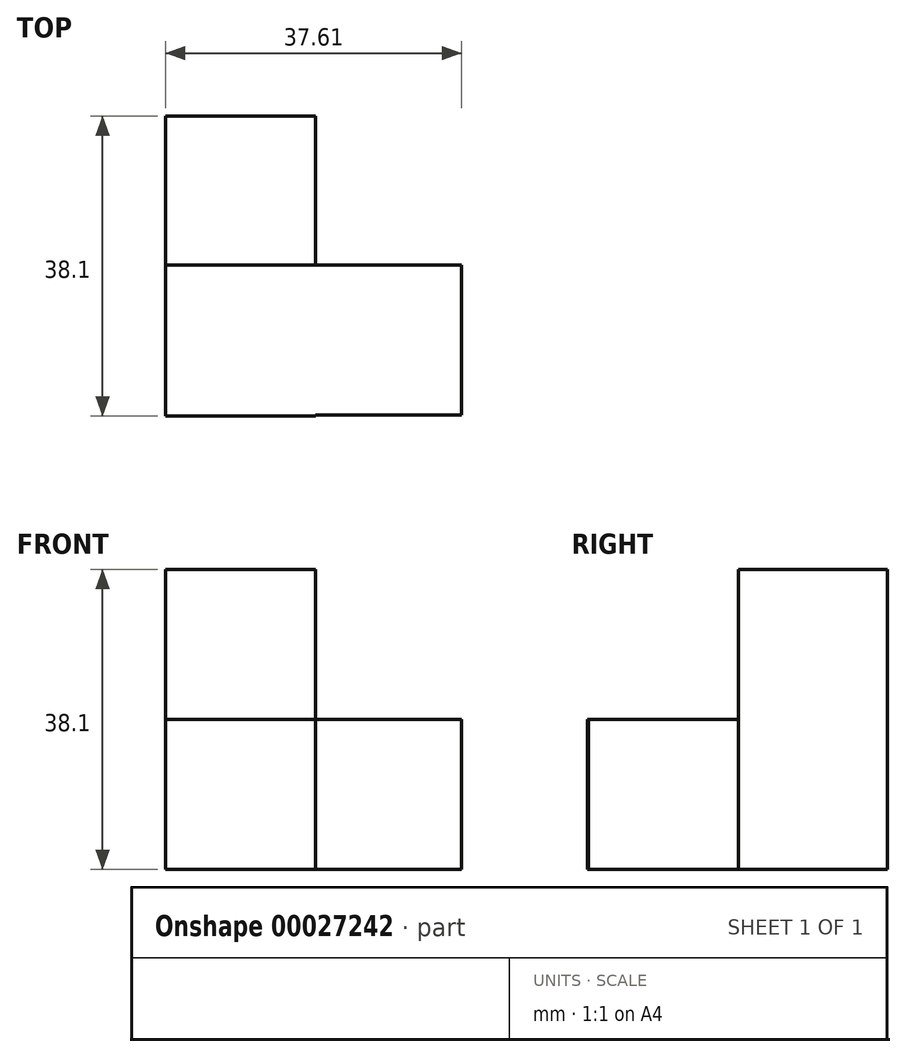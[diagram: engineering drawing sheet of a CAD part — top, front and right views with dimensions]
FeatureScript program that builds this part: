
annotation { "Feature Type Name" : "Feature", "Feature Type Description" : "" }
export const myFeature = defineFeature(function(context is Context, id is Id, definition is map)
    precondition{}
    {
        {
            var Q0;
            Q0=qCreatedBy(makeId("Top.planeOp"),FACE);
            var sketch = newSketch(context, id + "F0", { "sketchPlane" : qUnion([Q0])});
            skLineSegment(sketch, "E0.bottom", {"start": v(-37.6, 18.93) * mm, "end": v(-18.56, 18.93) * mm});
            skLineSegment(sketch, "E0.top", {"start": v(-37.6, -19.17) * mm, "end": v(-18.56, -19.17) * mm});
            skLineSegment(sketch, "E0.left", {"start": v(-37.6, 18.93) * mm, "end": v(-37.6, -19.17) * mm});
            skLineSegment(sketch, "E0.right", {"start": v(-18.56, 18.93) * mm, "end": v(-18.56, -19.17) * mm});
            skLineSegment(sketch, "E1.bottom", {"start": v(-19.05, -19.05) * mm, "end": v(0, -19.05) * mm});
            skLineSegment(sketch, "E1.top", {"start": v(-19.05, 0) * mm, "end": v(0, 0) * mm});
            skLineSegment(sketch, "E1.left", {"start": v(-19.05, -19.05) * mm, "end": v(-19.05, 0) * mm});
            skLineSegment(sketch, "E1.right", {"start": v(0, -19.05) * mm, "end": v(0, 0) * mm});
            skSolve(sketch);
        }
        {
            var Q0;
            {var subQ0=sQuery(id+"F0.wireOp",EDGE,"E1.right");Q0=makeQuery(id+"F0.imprint","IMPRINT",FACE,{"disambiguationData":[TD([[makeQuery(id+"F0.imprint","IMPRINT",EDGE,{"derivedFrom":subQ0}),1.0]])]});}
            var Q1;
            {var subQ0=sQuery(id+"F0.wireOp",EDGE,"E1.left");Q1=makeQuery(id+"F0.imprint","IMPRINT",FACE,{"disambiguationData":[TD([[makeQuery(id+"F0.imprint","IMPRINT",EDGE,{"derivedFrom":subQ0}),-1.0]])]});}
            var Q2;
            {var subQ7=sQuery(id+"F0.wireOp",EDGE,"E0.bottom");Q2=makeQuery(id+"F0.imprint","IMPRINT",FACE,{"disambiguationData":[TD([[makeQuery(id+"F0.imprint","IMPRINT",EDGE,{"derivedFrom":subQ7}),-1.0]])]});}
            extrude(context, id + "F1", {"entities" : qUnion([Q0, Q1, Q2]), "depth" : 19.05 * mm});
        }
        {
            var Q0;
            Q0=makeQuery(id+"F1.opExtrude","CAP_FACE",FACE,{"disambiguationData":[OSD([sQuery(id+"F0.wireOp",EDGE,"E0.bottom"),sQuery(id+"F0.wireOp",EDGE,"E0.top"),sQuery(id+"F0.wireOp",EDGE,"E0.left"),sQuery(id+"F0.wireOp",EDGE,"E0.right"),sQuery(id+"F0.wireOp",EDGE,"E1.bottom"),sQuery(id+"F0.wireOp",EDGE,"E1.top"),sQuery(id+"F0.wireOp",EDGE,"E1.right")])],"isStart":false});
            var sketch = newSketch(context, id + "F2", { "sketchPlane" : qUnion([Q0])});
            skLineSegment(sketch, "E2.bottom", {"start": v(-37.6, 18.93) * mm, "end": v(-18.56, 18.93) * mm});
            skLineSegment(sketch, "E2.top", {"start": v(-37.6, 0) * mm, "end": v(-18.56, 0) * mm});
            skLineSegment(sketch, "E2.left", {"start": v(-37.6, 18.93) * mm, "end": v(-37.6, 0) * mm});
            skLineSegment(sketch, "E2.right", {"start": v(-18.56, 18.93) * mm, "end": v(-18.56, 0) * mm});
            skSolve(sketch);
        }
        {
            var Q0;
            Q0=makeQuery(id+"F2.imprint","IMPRINT",FACE,{"disambiguationData":[TD([[makeQuery(id+"F2.imprint","IMPRINT",EDGE,{"derivedFrom":sQuery(id+"F2.wireOp",EDGE,"E2.bottom")}),-1.0]])]});
            extrude(context, id + "F3", {"entities" : qUnion([Q0]), "operationType" : NewBodyOperationType.ADD, "depth" : 19.05 * mm});
        }
    });
